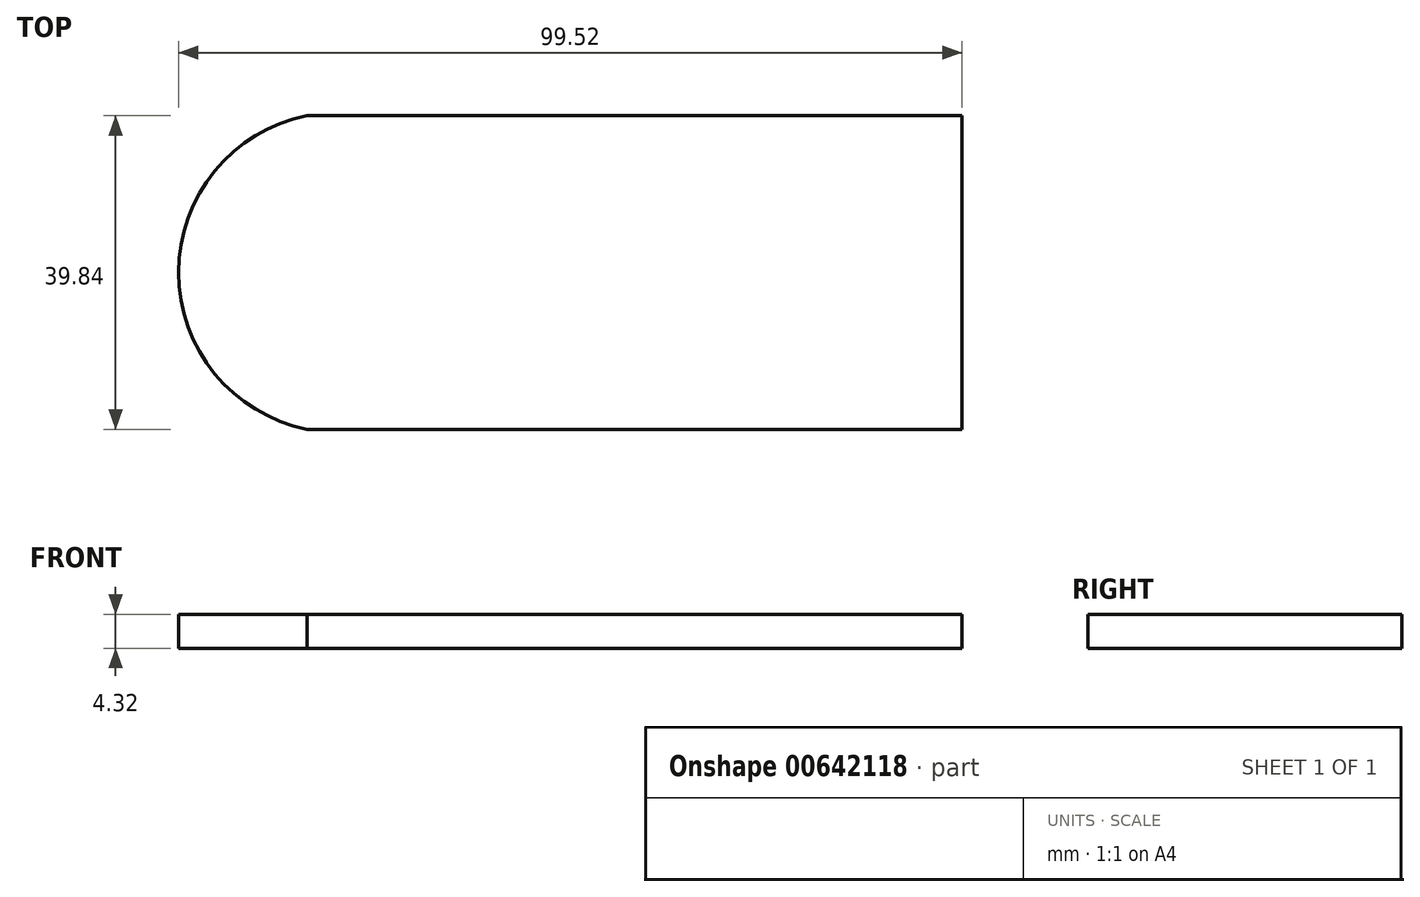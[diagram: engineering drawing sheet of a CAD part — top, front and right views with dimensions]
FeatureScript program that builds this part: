
annotation { "Feature Type Name" : "Feature", "Feature Type Description" : "" }
export const myFeature = defineFeature(function(context is Context, id is Id, definition is map)
    precondition{}
    {
        {
            var Q0;
            Q0=qCreatedBy(makeId("Top.planeOp"),FACE);
            var sketch = newSketch(context, id + "F0", { "sketchPlane" : qUnion([Q0])});
            skLineSegment(sketch, "E0", {"start": v(-39.4, 25.02) * mm, "end": v(43.81, 25.02) * mm});
            skLineSegment(sketch, "E1", {"start": v(-39.4, -14.82) * mm, "end": v(43.81, -14.82) * mm});
            skLineSegment(sketch, "E2", {"start": v(-35.39, 25.42) * mm, "end": v(-35.39, -15.22) * mm});
            skLineSegment(sketch, "E3", {"start": v(43.81, 25.02) * mm, "end": v(43.81, -14.82) * mm});
            skLineSegment(sketch, "E4", {"start": v(-60.5, 5.1) * mm, "end": v(72, 5.1) * mm, "construction": true});
            skPoint(sketch, "E4.startSnap0", {"position": v(-35.39, 5.1) * mm});
            skLineSegment(sketch, "E5", {"start": v(0, 37.5) * mm, "end": v(0, -37.82) * mm});
            skArc(sketch, "E6", {"start": v(-39.4, 25.02) * mm, "mid": v(-55.7, 5.1) * mm, "end": v(-39.4, -14.82) * mm});
            skPoint(sketch, "E7.orphan", {"position": v(-35.39, 25.02) * mm});
            skPoint(sketch, "E8.orphan", {"position": v(-35.39, -14.82) * mm});
            skSolve(sketch);
        }
        {
            var Q0;
            {var subQ0=sQuery(id+"F0.wireOp",EDGE,"E6");Q0=makeQuery(id+"F0.imprint","IMPRINT",FACE,{"disambiguationData":[TD([[makeQuery(id+"F0.imprint","IMPRINT",EDGE,{"derivedFrom":subQ0}),1.0]])]});}
            extrude(context, id + "F1", {"entities" : qUnion([Q0]), "depth" : 4.32 * mm, "offsetDistance" : 25.4 * mm});
        }
        {
            var Q0;
            {var subQ0=sQuery(id+"F0.wireOp",EDGE,"E2");var subQ1=sQuery(id+"F0.wireOp",EDGE,"E0");var subQ2=makeQuery(id+"F0.imprint","INTERSECT",VERTEX,{"derivedFrom":[subQ1,subQ0]});Q0=makeQuery(id+"F0.imprint","IMPRINT",FACE,{"disambiguationData":[TD([[makeQuery(id+"F0.imprint","IMPRINT",EDGE,{"disambiguationData":[TD([[subQ2,-1.0]])],"derivedFrom":subQ1}),-1.0]])]});}
            var Q1;
            {var subQ0=sQuery(id+"F0.wireOp",EDGE,"E3");Q1=makeQuery(id+"F0.imprint","IMPRINT",FACE,{"disambiguationData":[TD([[makeQuery(id+"F0.imprint","IMPRINT",EDGE,{"derivedFrom":subQ0}),-1.0]])]});}
            extrude(context, id + "F2", {"entities" : qUnion([Q0, Q1]), "operationType" : NewBodyOperationType.ADD, "depth" : 4.32 * mm, "offsetDistance" : 25.4 * mm});
        }
    });
